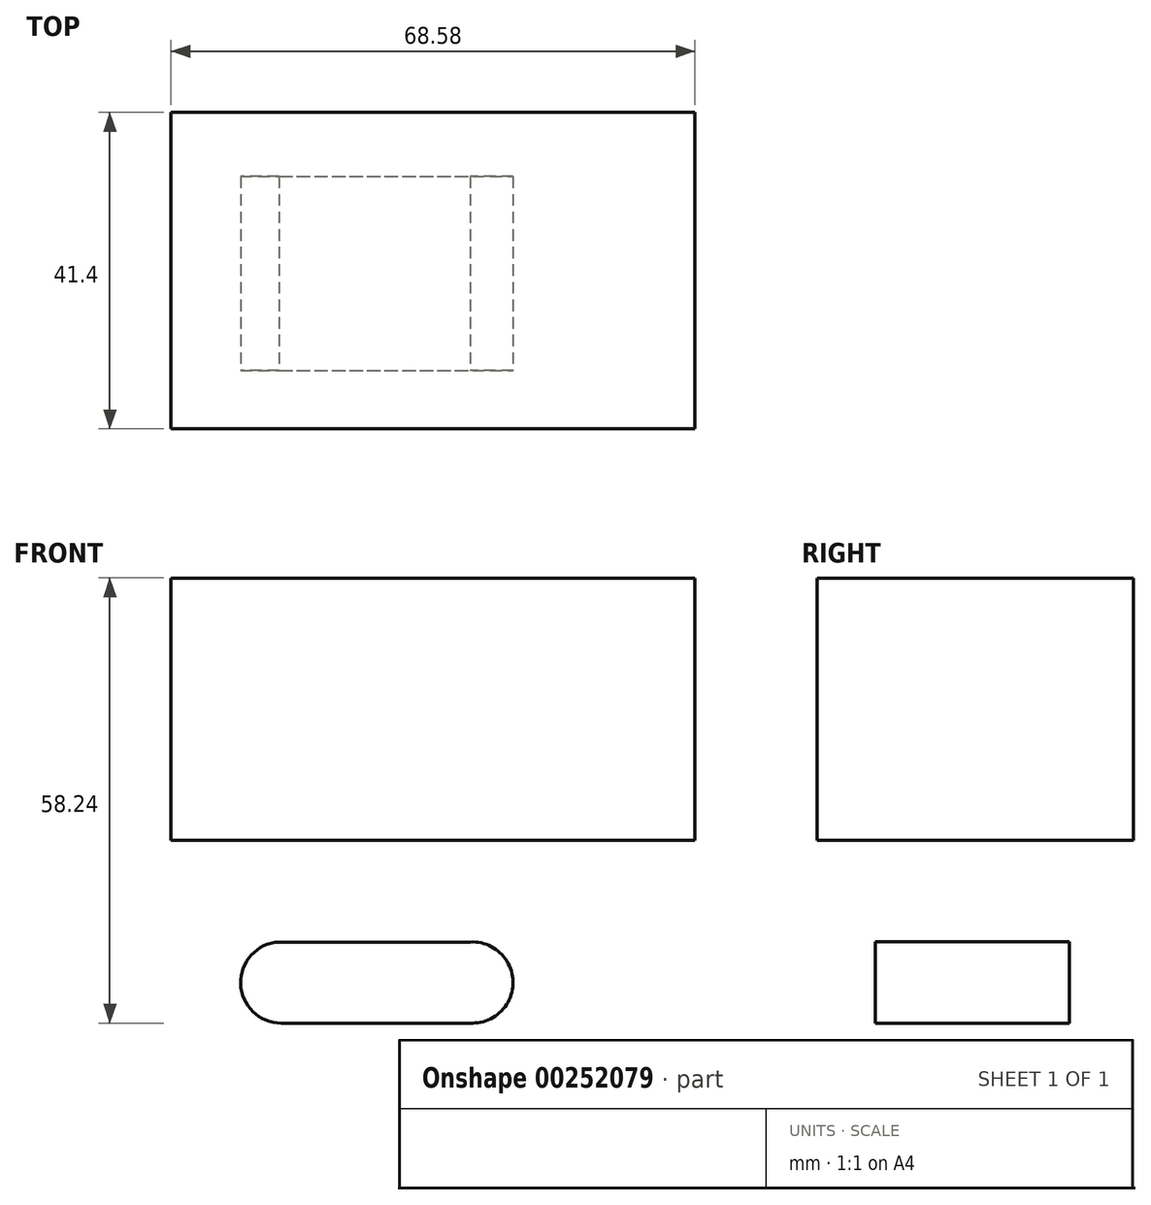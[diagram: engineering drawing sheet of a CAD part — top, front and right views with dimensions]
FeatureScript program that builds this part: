
annotation { "Feature Type Name" : "Feature", "Feature Type Description" : "" }
export const myFeature = defineFeature(function(context is Context, id is Id, definition is map)
    precondition{}
    {
        {
            var Q0;
            Q0=qCreatedBy(makeId("Front.planeOp"),FACE);
            var sketch = newSketch(context, id + "F0", { "sketchPlane" : qUnion([Q0])});
            skLineSegment(sketch, "E0.bottom", {"start": v(39.73, -46.8) * mm, "end": v(-39.73, -46.8) * mm});
            skLineSegment(sketch, "E0.top", {"start": v(39.73, 46.8) * mm, "end": v(-39.73, 46.8) * mm});
            skLineSegment(sketch, "E0.left", {"start": v(39.73, -46.8) * mm, "end": v(39.73, 46.8) * mm});
            skLineSegment(sketch, "E0.right", {"start": v(-39.73, -46.8) * mm, "end": v(-39.73, 46.8) * mm});
            skPoint(sketch, "E0.middle", {"position": v(0, 0) * mm});
            skSolve(sketch);
        }
        {
            var Q0;
            Q0=makeQuery(id+"F0.imprint","IMPRINT",FACE,{"disambiguationData":[TD([[makeQuery(id+"F0.imprint","IMPRINT",EDGE,{"derivedFrom":sQuery(id+"F0.wireOp",EDGE,"E0.bottom")}),-1.0]])]});
            extrude(context, id + "F1", {"entities" : qUnion([Q0]), "depth" : 25.4 * mm});
        }
        {
            var Q0;
            Q0=makeQuery(id+"F1.opExtrude","CAP_FACE",FACE,{"disambiguationData":[OSD([sQuery(id+"F0.wireOp",EDGE,"E0.bottom"),sQuery(id+"F0.wireOp",EDGE,"E0.top"),sQuery(id+"F0.wireOp",EDGE,"E0.left"),sQuery(id+"F0.wireOp",EDGE,"E0.right")])],"isStart":false});
            var sketch = newSketch(context, id + "F2", { "sketchPlane" : qUnion([Q0])});
            skLineSegment(sketch, "E1", {"start": v(-12.8, 30.48) * mm, "end": v(12.25, 30.48) * mm});
            skLineSegment(sketch, "E2", {"start": v(-12.52, 41.1) * mm, "end": v(12.52, 41.1) * mm});
            skArc(sketch, "E3", {"start": v(12.25, 30.48) * mm, "mid": v(17.83, 35.65) * mm, "end": v(12.52, 41.1) * mm});
            skArc(sketch, "E4", {"start": v(-12.52, 41.1) * mm, "mid": v(-17.83, 35.92) * mm, "end": v(-12.8, 30.48) * mm});
            skArc(sketch, "E5.MirrorCS", {"start": v(12.25, -30.48) * mm, "mid": v(17.83, -35.65) * mm, "end": v(12.52, -41.1) * mm});
            skLineSegment(sketch, "E6.MirrorCS", {"start": v(-12.52, -41.1) * mm, "end": v(12.52, -41.1) * mm});
            skLineSegment(sketch, "E7.MirrorCS", {"start": v(-12.8, -30.48) * mm, "end": v(12.25, -30.48) * mm});
            skArc(sketch, "E8.MirrorCS", {"start": v(-12.52, -41.1) * mm, "mid": v(-17.83, -35.92) * mm, "end": v(-12.8, -30.48) * mm});
            skSolve(sketch);
        }
        {
            var Q0;
            Q0=makeQuery(id+"F2.imprint","IMPRINT",FACE,{"disambiguationData":[TD([[makeQuery(id+"F2.imprint","IMPRINT",EDGE,{"derivedFrom":sQuery(id+"F2.wireOp",EDGE,"E1")}),1.0]])]});
            var Q1;
            Q1=makeQuery(id+"F2.imprint","IMPRINT",FACE,{"disambiguationData":[TD([[makeQuery(id+"F2.imprint","IMPRINT",EDGE,{"derivedFrom":sQuery(id+"F2.wireOp",EDGE,"E5.MirrorCS")}),-1.0]])]});
            extrude(context, id + "F3", {"entities" : qUnion([Q0, Q1]), "operationType" : NewBodyOperationType.REMOVE, "oppositeDirection" : true, "depth" : 50.3 * mm});
        }
        {
            var Q0;
            Q0=qCreatedBy(makeId("Front.planeOp"),FACE);
            var sketch = newSketch(context, id + "F4", { "sketchPlane" : qUnion([Q0])});
            skLineSegment(sketch, "E9", {"start": v(-26.4, 36.16) * mm, "end": v(-42.18, 48.44) * mm});
            skLineSegment(sketch, "E10", {"start": v(-26.4, 36.16) * mm, "end": v(-26.4, -36.16) * mm});
            skLineSegment(sketch, "E11", {"start": v(-44.63, -50.35) * mm, "end": v(-26.4, -36.16) * mm});
            skLineSegment(sketch, "E12", {"start": v(-42.18, 48.44) * mm, "end": v(-44.63, -50.35) * mm});
            skSolve(sketch);
        }
        {
            var Q0;
            Q0=makeQuery(id+"F4.imprint","IMPRINT",FACE,{"disambiguationData":[TD([[makeQuery(id+"F4.imprint","IMPRINT",EDGE,{"derivedFrom":sQuery(id+"F4.wireOp",EDGE,"E9")}),-1.0]])]});
            var Q1;
            Q1=makeQuery(id+"F4.imprint","IMPRINT",FACE,{"disambiguationData":[TD([[makeQuery(id+"F4.imprint","IMPRINT",EDGE,{"derivedFrom":sQuery(id+"F4.wireOp",EDGE,"E9")}),1.0]])]});
            extrude(context, id + "F5", {"entities" : qUnion([Q0, Q1]), "operationType" : NewBodyOperationType.REMOVE, "depth" : 133.1 * mm});
        }
        {
            var Q0;
            Q0=qCreatedBy(makeId("Front.planeOp"),FACE);
            var sketch = newSketch(context, id + "F6", { "sketchPlane" : qUnion([Q0])});
            skLineSegment(sketch, "E13.bottom", {"start": v(-26.94, -17.15) * mm, "end": v(41.64, -17.15) * mm});
            skLineSegment(sketch, "E13.top", {"start": v(-26.94, 17.15) * mm, "end": v(41.64, 17.15) * mm});
            skLineSegment(sketch, "E13.left", {"start": v(-26.94, -17.15) * mm, "end": v(-26.94, 17.15) * mm});
            skLineSegment(sketch, "E13.right", {"start": v(41.64, -17.15) * mm, "end": v(41.64, 17.15) * mm});
            skPoint(sketch, "E13.middle", {"position": v(7.35, 0) * mm});
            skSolve(sketch);
        }
        {
            var Q0;
            Q0=makeQuery(id+"F6.imprint","IMPRINT",FACE,{"disambiguationData":[TD([[makeQuery(id+"F6.imprint","IMPRINT",EDGE,{"derivedFrom":sQuery(id+"F6.wireOp",EDGE,"E13.bottom")}),1.0]])]});
            extrude(context, id + "F7", {"entities" : qUnion([Q0]), "operationType" : NewBodyOperationType.ADD, "oppositeDirection" : true, "depth" : 8.38 * mm});
        }
        {
            var Q0;
            Q0=makeQuery(id+"F7.opExtrude","CAP_FACE",FACE,{"disambiguationData":[OSD([sQuery(id+"F6.wireOp",EDGE,"E13.bottom"),sQuery(id+"F6.wireOp",EDGE,"E13.top"),sQuery(id+"F6.wireOp",EDGE,"E13.left"),sQuery(id+"F6.wireOp",EDGE,"E13.right")])],"isStart":false});
            extrude(context, id + "F8", {"entities" : qUnion([Q0]), "operationType" : NewBodyOperationType.ADD, "oppositeDirection" : true, "depth" : 41.4 * mm});
        }
    });
